# Revit family: Condensing-Storage-Water-Heater-Gas_AO_Smith-BFC_120_PG
name_source: partatom
category: Mechanical Equipment
revit_build: Autodesk Revit 2014 (Build: 20130308_1515(x64)
units: mm (PartAtom-declared; Revit-internal decimal feet)

## types (1)
- Condensing-Storage-Water-Heater-Gas_AO_Smith-BFC_120_PG
    (Additional Control) Frequency = 0 Hz
    (Additional Control) Phase = 1
    (Additional Control) Power Consumption (nominal) = 0 W
    (Additional Control) Voltage = 0 V
    1e Maintenance (check-up) = 3 months after installation
    2nd Maintenance (general maintenance) = 12 months after installation
    APS Pressure < = 210.0 Pa
    Assembly Code = D3010
    BIM Content Developer = CAD & Company
    CE-PIN = 0063BU3889
    Co2 Emissions (tol. +/- 1.0) vol% = 9.6
    Cold Water Connection R = 1 1/2"
    Condens Discharge Connection = 40 mm  [stored 0.131234 ft]
    Default Setpoint = 65 °C
    Description = Condensing High Efficiency Storage Water Heater
    Destination / Country = UK & Ireland
    Diameter = 850 mm  [stored 2.78871 ft]
    Drain Valve Connection Rp = 3/4"
    Draw-off Capacity @ ΔT = 28°C after 120 min. = 8000.0 L
    Draw-off Capacity @ ΔT = 28°C after 30 min. = 2400.0 L
    Draw-off Capacity @ ΔT = 28°C after 60 min. = 4300.0 L
    Draw-off Capacity @ ΔT = 28°C after 90 min. = 6100.0 L
    Draw-off Capacity @ ΔT = 44°C after 120 min. = 5000.0 L
    Draw-off Capacity @ ΔT = 44°C after 30 min. = 1500.0 L
    Draw-off Capacity @ ΔT = 44°C after 60 min. = 2600.0 L
    Draw-off Capacity @ ΔT = 44°C after 90 min. = 3800.0 L
    Draw-off Capacity @ ΔT = 50°C after 120 min. = 4400.0 L
    Draw-off Capacity @ ΔT = 50°C after 30 min. = 1300.0 L
    Draw-off Capacity @ ΔT = 50°C after 60 min. = 2300.0 L
    Draw-off Capacity @ ΔT = 50°C after 90 min. = 3400.0 L
    Draw-off Capacity @ ΔT = 55°C after 120 min. = 4000.0 L
    Draw-off Capacity @ ΔT = 55°C after 30 min. = 1100.0 L
    Draw-off Capacity @ ΔT = 55°C after 60 min. = 2100.0 L
    Draw-off Capacity @ ΔT = 55°C after 90 min. = 3000.0 L
    Draw-off Capacity @ ΔT = 70°C after 120 min. = 3000.0 L
    Draw-off Capacity @ ΔT = 70°C after 30 min. = 760.0 L
    Draw-off Capacity @ ΔT = 70°C after 60 min. = 1600.0 L
    Draw-off Capacity @ ΔT = 70°C after 90 min. = 2300.0 L
    Empty Weight = 480 kg
    Energy Efficiency Rating (Hi, acc NEN-EN 89-1999) = 105
    Energy Efficiency Rating (Hs, acc NEN-EN 89-1999) = 95
    Flue Diameter - concentric system = 130/200 mm/mm
    Flue Diameter - parallel system = 130 mm  [stored 0.426509 ft]
    Flue Diameter - water heater = 130/200 mm/mm
    Frequency = 50 Hz
    Gas Category = II2H3P
    Gas Connection R = 3/4"
    Gas Flow Rate - Mass kg/h = 9
    Gas Flow Rate - Volume ltr/hr = 0
    Heating Up Time @ ΔT = 28°C = 8
    Heating Up Time @ ΔT = 44°C = 12
    Heating Up Time @ ΔT = 50°C = 14
    Heating Up Time @ ΔT = 55°C = 15
    Heating Up Time @ ΔT = 70°C = 19
    Height = 2060 mm  [stored 6.75853 ft]
    Height Air Inlet = 1995 mm  [stored 6.54528 ft]
    Height Cold water Intlet = 225 mm  [stored 0.738189 ft]
    Height Flue Outlet = 1995 mm  [stored 6.54528 ft]
    Height Gas Connection = 1855 mm  [stored 6.08596 ft]
    Height Warm Water Outlet = 2060 mm  [stored 6.75853 ft]
    Hot / Warm Water Connection R = 1 1/2"
    Installation Type = B23/C13/C33/C43/C53/C63
    Insulation Thickness = 44 mm  [stored 0.144357 ft]
    Length = 900 mm  [stored 2.95276 ft]
    Maintenance Interval = 12 months
    Manufacturer = A.O. Smith Water Products Company b.v.
    Manufacturer Number = E 7110
    Max. Flue Gas Outlet Temperature = 60 °C
    Max. Operating Pressure = 800000.0 Pa
    Max. Setpoint = 80 °C
    Min. Setpoint = 40 °C
    Model = BFC 120 PG
    NOx Emissions (air free, 0% O2) ppm = 26
    NOx Emissions mg/kWh = 47
    Noice-level dB (A) = 45
    Nominal Heat Input (Gross) = 126100 W
    Nominal Heat Input (Net) = 116000 W
    Nominal Output = 121800 W
    Operating Weight = 960 kg
    Packaging Height = 2060 mm  [stored 6.75853 ft]
    Packaging Length = 1020 mm  [stored 3.34646 ft]
    Packaging Width = 920 mm  [stored 3.01837 ft]
    Phase = 1
    Power Consumption (nominal) = 240 W
    Product Documentation Link = http://www.aosmithinternational.com
    Product Instruction Link = http://www.aosmith.co.uk
    Recovery Rate @ ΔT = 28°C = 3800.0 L/s
    Recovery Rate @ ΔT = 44°C = 2400.0 L/s
    Recovery Rate @ ΔT = 50°C = 2100.0 L/s
    Recovery Rate @ ΔT = 55°C = 2000.0 L/s
    Recovery Rate @ ΔT = 70°C = 1500.0 L/s
    Seasonal Energy Efficiency Rating = 95
    Serial Number = 8717449250263
    Stand-by Loss = 0 W
    Stand-by Loss - daily (24h) = 0 W
    Standard Set For = G31
    Storage Capacity = 480.0 L
    Supply Pressure min/max = 3700 - 5000 Pa
    T&P Connection Rp = 1"
    Transport Weight = 501 kg
    Type of Packaging = Plastic Shrink Wrap, Cardboard and Wood
    URL = www.aosmith.co.uk
    Voltage = 230 V
    Warranty on parts = 12 months
    Warranty on tank = 36 months
    Width = 1000 mm  [stored 3.28084 ft]

note: [stored X ft] marks values corroborated as IEEE doubles in the binary element streams (Revit-internal decimal feet)

## geometry (parser evidence)
native form markers: Blend x19, Sweep x44
no freeform markers — native parametric forms only
